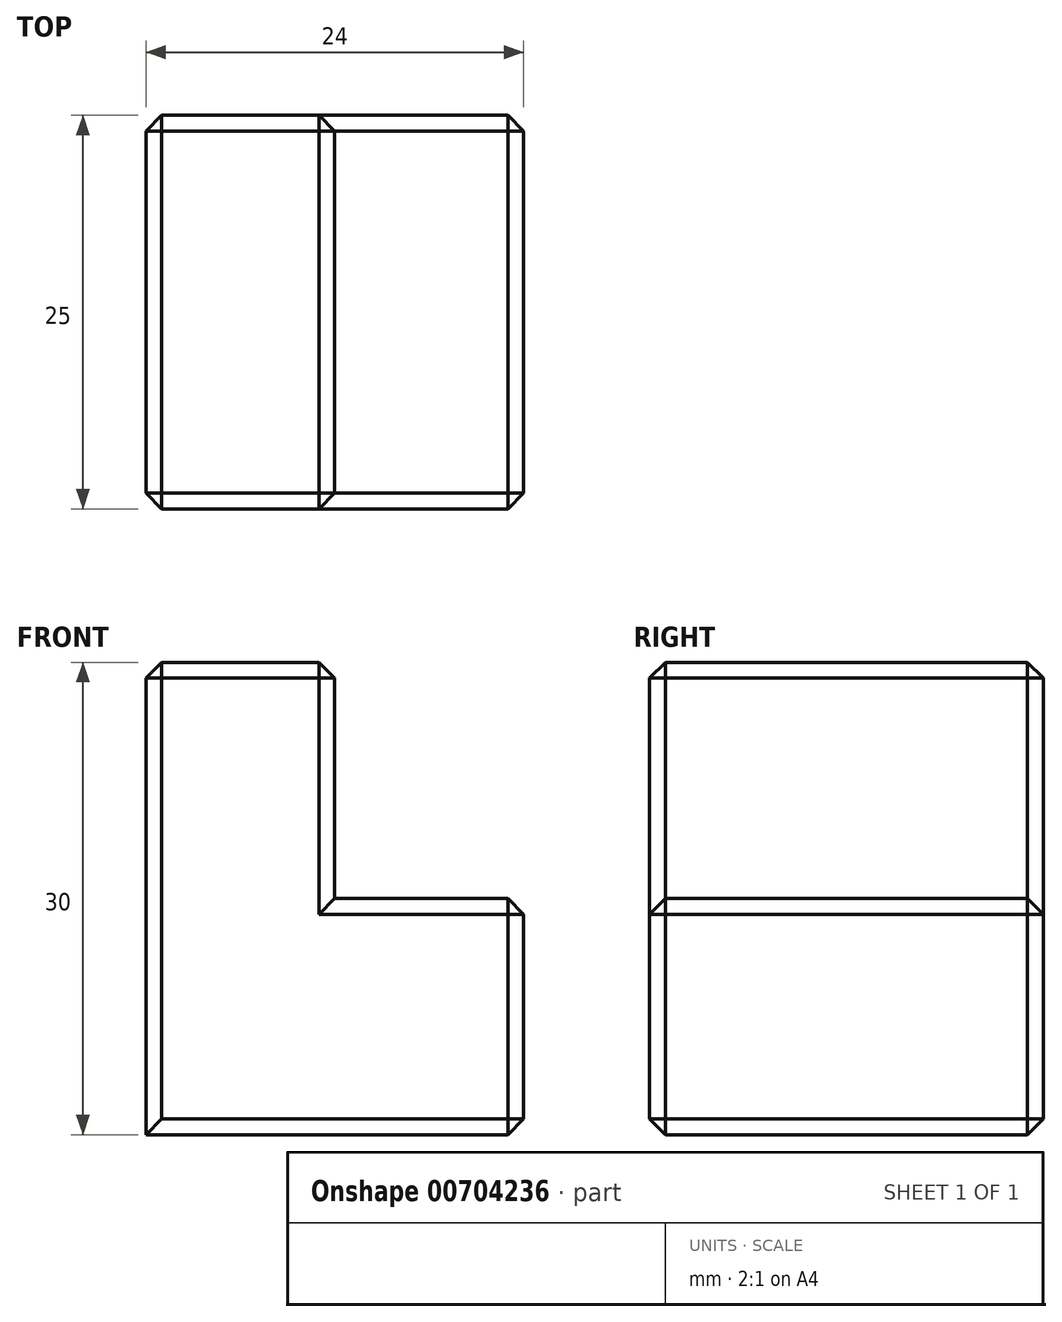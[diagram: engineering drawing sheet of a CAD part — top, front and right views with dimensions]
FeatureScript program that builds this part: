
annotation { "Feature Type Name" : "Feature", "Feature Type Description" : "" }
export const myFeature = defineFeature(function(context is Context, id is Id, definition is map)
    precondition{}
    {
        {
            var Q0;
            Q0=qCreatedBy(makeId("Front.planeOp"),FACE);
            var sketch = newSketch(context, id + "F0", { "sketchPlane" : qUnion([Q0])});
            skLineSegment(sketch, "E0", {"start": v(0, 0) * mm, "end": v(0, 15) * mm});
            skLineSegment(sketch, "E1", {"start": v(0, 15) * mm, "end": v(-12, 15) * mm});
            skLineSegment(sketch, "E2", {"start": v(-12, 15) * mm, "end": v(-12, -15) * mm});
            skLineSegment(sketch, "E3", {"start": v(-12, -15) * mm, "end": v(12, -15) * mm});
            skLineSegment(sketch, "E4", {"start": v(12, -15) * mm, "end": v(12, 0) * mm});
            skLineSegment(sketch, "E5", {"start": v(12, 0) * mm, "end": v(0, 0) * mm});
            skSolve(sketch);
        }
        {
            var Q0;
            Q0 = qSketchRegion(id + "F0", true);
            extrude(context, id + "F1", {"entities" : qUnion([Q0]), "depth" : 25 * mm, "offsetDistance" : 25 * mm});
        }
        {
            var Q0;
            Q0=makeQuery(id+"F1.opExtrude","CAP_FACE",FACE,{"disambiguationData":[OSD([sQuery(id+"F0.wireOp",EDGE,"E0"),sQuery(id+"F0.wireOp",EDGE,"E1"),sQuery(id+"F0.wireOp",EDGE,"E2"),sQuery(id+"F0.wireOp",EDGE,"E3"),sQuery(id+"F0.wireOp",EDGE,"E4"),sQuery(id+"F0.wireOp",EDGE,"E5")])],"isStart":false});
            var Q1;
            Q1=makeQuery(id+"F1.opExtrude","CAP_FACE",FACE,{"disambiguationData":[OSD([sQuery(id+"F0.wireOp",EDGE,"E0"),sQuery(id+"F0.wireOp",EDGE,"E1"),sQuery(id+"F0.wireOp",EDGE,"E2"),sQuery(id+"F0.wireOp",EDGE,"E3"),sQuery(id+"F0.wireOp",EDGE,"E4"),sQuery(id+"F0.wireOp",EDGE,"E5")])],"isStart":true});
            var Q2;
            Q2=makeQuery(id+"F1.opExtrude","SWEPT_FACE",FACE,{"disambiguationData":[OSD([sQuery(id+"F0.wireOp",EDGE,"E1")])]});
            var Q3;
            Q3=makeQuery(id+"F1.opExtrude","SWEPT_FACE",FACE,{"disambiguationData":[OSD([sQuery(id+"F0.wireOp",EDGE,"E4")])]});
            chamfer(context, id + "F2", {"entities" : qUnion([Q0, Q1, Q2, Q3]), "width" : 1 * mm, "tangentPropagation" : true});
        }
    });
